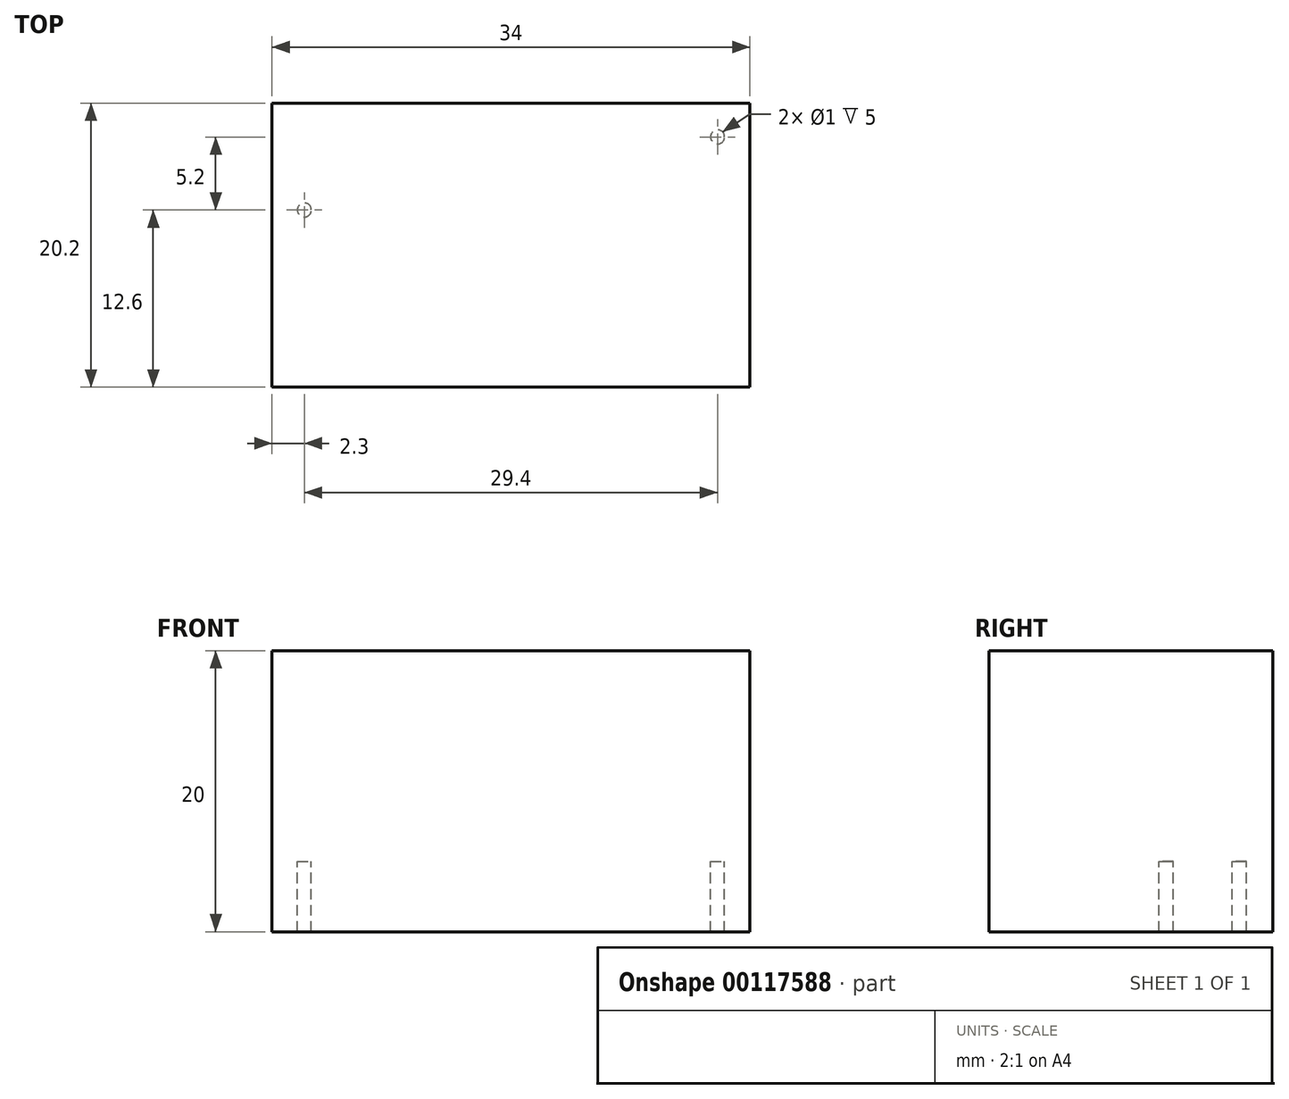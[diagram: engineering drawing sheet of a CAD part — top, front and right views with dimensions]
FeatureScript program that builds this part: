
annotation { "Feature Type Name" : "Feature", "Feature Type Description" : "" }
export const myFeature = defineFeature(function(context is Context, id is Id, definition is map)
    precondition{}
    {
        {
            var Q0;
            Q0=qCreatedBy(makeId("Front.planeOp"),FACE);
            var sketch = newSketch(context, id + "F0", { "sketchPlane" : qUnion([Q0])});
            skLineSegment(sketch, "E0", {"start": v(-17, 0) * mm, "end": v(17, 0) * mm});
            skLineSegment(sketch, "E1", {"start": v(17, 0) * mm, "end": v(17, 15) * mm});
            skLineSegment(sketch, "E2", {"start": v(17, 15) * mm, "end": v(-17, 15) * mm});
            skLineSegment(sketch, "E3", {"start": v(-17, 15) * mm, "end": v(-17, 0) * mm});
            skSolve(sketch);
        }
        {
            var Q0;
            Q0=makeQuery(id+"F0.imprint","IMPRINT",FACE,{"disambiguationData":[TD([[makeQuery(id+"F0.imprint","IMPRINT",EDGE,{"derivedFrom":sQuery(id+"F0.wireOp",EDGE,"E0")}),1.0]])]});
            extrude(context, id + "F1", {"entities" : qUnion([Q0]), "endBound" : BoundingType.SYMMETRIC, "depth" : 20.2 * mm});
        }
        {
            var Q0;
            Q0=makeQuery(id+"F1.opExtrude","SWEPT_FACE",FACE,{"disambiguationData":[OSD([sQuery(id+"F0.wireOp",EDGE,"E0")])]});
            var sketch = newSketch(context, id + "F2", { "sketchPlane" : qUnion([Q0])});
            skCircle(sketch, "E4", {"center": v(-14.7, 2.5) * mm, "radius": 0.5 * mm});
            skCircle(sketch, "E5", {"center": v(14.7, 7.7) * mm, "radius": 0.5 * mm});
            skLineSegment(sketch, "E6", {"start": v(-14.7, 2.5) * mm, "end": v(14.7, 2.5) * mm, "construction": true});
            skLineSegment(sketch, "E7", {"start": v(0, 2.5) * mm, "end": v(0, 10.1) * mm, "construction": true});
            skCircle(sketch, "E8.MirrorC", {"center": v(14.7, -7.7) * mm, "radius": 0.5 * mm});
            skCircle(sketch, "E9.MirrorC", {"center": v(-14.7, -2.5) * mm, "radius": 0.5 * mm});
            skSolve(sketch);
        }
        {
            var Q0;
            Q0=makeQuery(id+"F2.imprint","IMPRINT",FACE,{"disambiguationData":[TD([[makeQuery(id+"F2.imprint","IMPRINT",EDGE,{"derivedFrom":sQuery(id+"F2.wireOp",EDGE,"E4")}),1.0]])]});
            var Q1;
            Q1=makeQuery(id+"F2.imprint","IMPRINT",FACE,{"disambiguationData":[TD([[makeQuery(id+"F2.imprint","IMPRINT",EDGE,{"derivedFrom":sQuery(id+"F2.wireOp",EDGE,"E9.MirrorC")}),-1.0]])]});
            var Q2;
            Q2=makeQuery(id+"F2.imprint","IMPRINT",FACE,{"disambiguationData":[TD([[makeQuery(id+"F2.imprint","IMPRINT",EDGE,{"derivedFrom":sQuery(id+"F2.wireOp",EDGE,"E5")}),1.0]])]});
            var Q3;
            Q3=makeQuery(id+"F2.imprint","IMPRINT",FACE,{"disambiguationData":[TD([[makeQuery(id+"F2.imprint","IMPRINT",EDGE,{"derivedFrom":sQuery(id+"F2.wireOp",EDGE,"E8.MirrorC")}),-1.0]])]});
            extrude(context, id + "F3", {"entities" : qUnion([Q0, Q1, Q2, Q3]), "operationType" : NewBodyOperationType.ADD, "depth" : 5 * mm});
        }
    });
